# Revit family: ToiletPaperDispenser_Metlam_DoubleJumbo
name_source: partatom
category: Generic Models
revit_build: Autodesk Revit Architecture 2013 (Build: 20120221_2030(x64)
units: mm (PartAtom-declared; Revit-internal decimal feet)

## types (1)
- Metlam Double Jumbo TPD
    Assembly Code = E1090900
    Default Elevation = 1219 mm
    Depth = 150 mm
    Description = SS Double Large Toilet Roll Dispenser
    FilterObject_ANZRS = Toilet Paper Dispenser
    Height = 284 mm  [stored 0.931759 ft]
    Keywords = CAPACITY 2 Standard Rolls up to 108mm wide sheet x 300mm long
    Manufacturer = Metlam
    Material = Stainless Steel, Satin
    Model = Double Jumbo
    ModifiedIssue_ANZRS = 130318.01 $
    Product Code = ML 841 DBL
    StyleOrType_ANZRS = Sanitary Ware
    URL = http://www.metlam.com.au
    Width = 520 mm  [stored 1.70604 ft]

note: [stored X ft] marks values corroborated as IEEE doubles in the binary element streams (Revit-internal decimal feet)

## geometry (parser evidence)
native form markers: Blend x28, Extrusion x1, Sweep x1
no freeform markers — native parametric forms only
